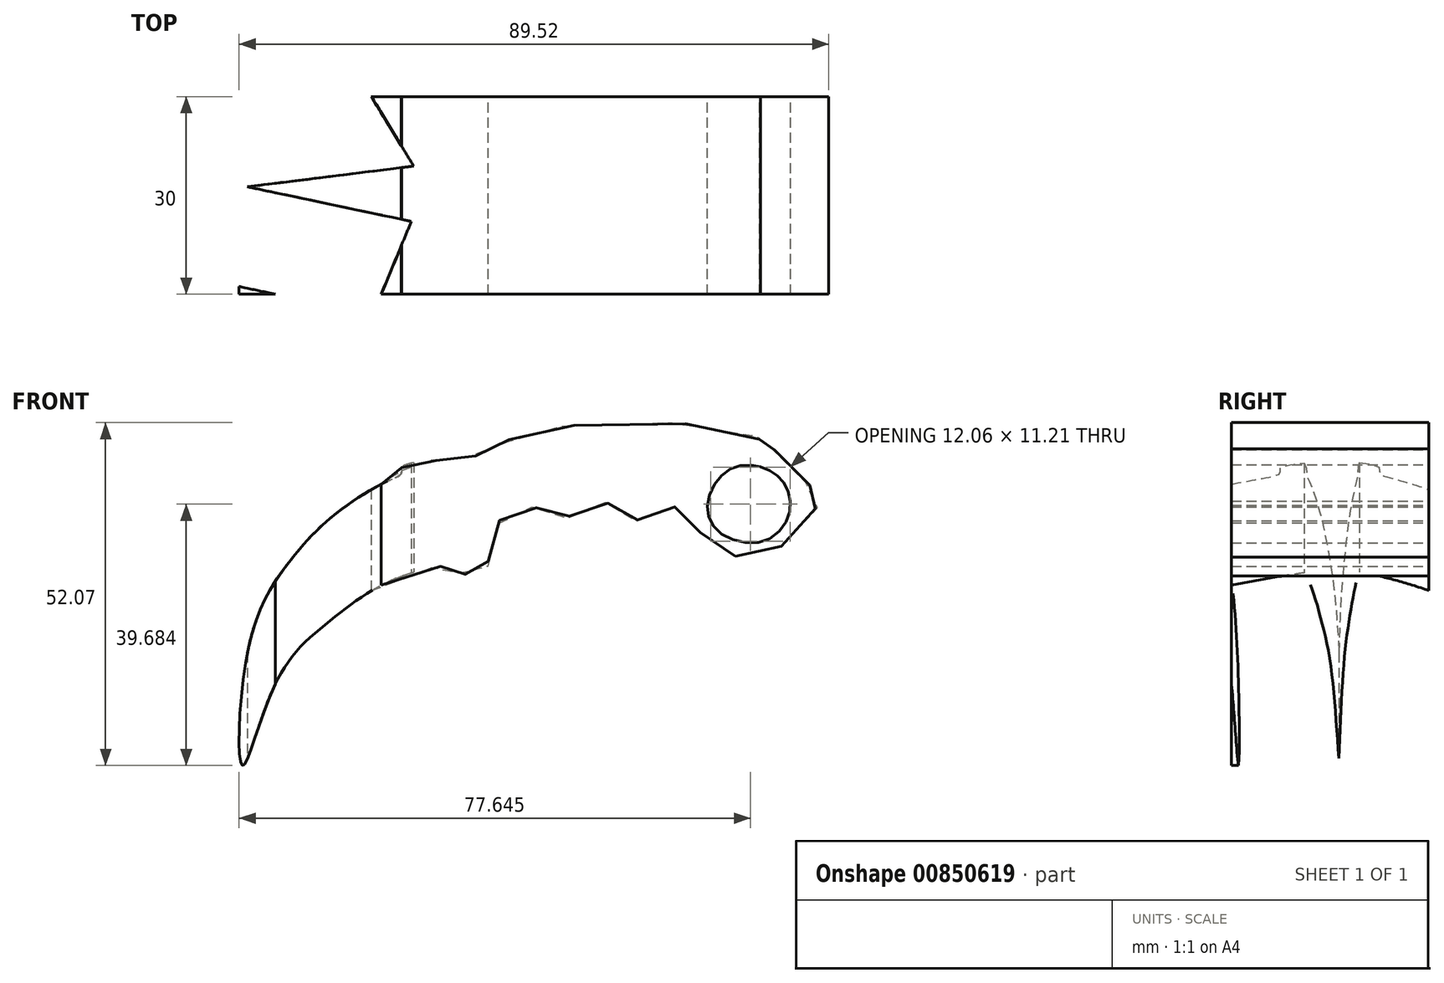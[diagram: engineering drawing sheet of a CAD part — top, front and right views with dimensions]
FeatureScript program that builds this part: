
annotation { "Feature Type Name" : "Feature", "Feature Type Description" : "" }
export const myFeature = defineFeature(function(context is Context, id is Id, definition is map)
    precondition{}
    {
        {
            var Q0;
            Q0=qCreatedBy(makeId("Front.planeOp"),FACE);
            var sketch = newSketch(context, id + "F0", { "sketchPlane" : qUnion([Q0])});
            skFitSpline(sketch, "E0", {"points": [v(33.88, 44.4) * mm, v(30.64, 46.68) * mm, v(25.88, 46.49) * mm, v(22.46, 41.73) * mm, v(23.98, 36.97) * mm, v(30.83, 35.45) * mm, v(34.83, 39.83) * mm, v(33.88, 44.4) * mm]});
            skFitSpline(sketch, "E1", {"points": [v(-48.25, 1.4) * mm, v(-43.13, 14.07) * mm, v(-34.97, 23.36) * mm, v(-27.13, 28.8) * mm, v(-17.69, 31.67) * mm, v(-15.29, 31.2) * mm, v(-15.13, 30.72) * mm, v(-11.29, 30.4) * mm, v(-10.97, 32) * mm, v(-9.7, 37.3) * mm, v(-8.41, 39.54) * mm, v(-3.45, 40.5) * mm, v(0, 38.56) * mm, v(3.27, 40.8) * mm, v(7.76, 40.96) * mm, v(10.96, 38.23) * mm, v(13.36, 40.31) * mm, v(18, 40.47) * mm, v(19.93, 38.54) * mm, v(23.61, 34.53) * mm, v(27.61, 33.08) * mm, v(33.54, 34.68) * mm, v(38.02, 39.97) * mm, v(40.74, 41.73) * mm, v(34.17, 46.7) * mm, v(32.24, 49.44) * mm, v(30.32, 49.44) * mm, v(30.32, 50.72) * mm, v(12.87, 53.47) * mm, v(-7.3, 51.24) * mm, v(-8.74, 49.96) * mm, v(-13.86, 48.2) * mm, v(-18.02, 47.73) * mm, v(-21.22, 47.57) * mm, v(-24.1, 46.61) * mm, v(-24.1, 45.8) * mm, v(-26.35, 44.53) * mm, v(-32.27, 41) * mm, v(-36.9, 37.16) * mm, v(-41.86, 31.4) * mm, v(-47.46, 18.73) * mm, v(-48.25, 1.4) * mm]});
            skSolve(sketch);
        }
        {
            var Q0;
            Q0 = qSketchRegion(id + "F0", true);
            extrude(context, id + "F1", {"entities" : qUnion([Q0]), "depth" : 30 * mm, "offsetDistance" : 25 * mm});
        }
        {
            var Q0;
            Q0=qCreatedBy(makeId("Top.planeOp"),FACE);
            var sketch = newSketch(context, id + "F2", { "sketchPlane" : qUnion([Q0])});
            skLineSegment(sketch, "E2", {"start": v(-22.61, -18.94) * mm, "end": v(-47.5, -13.69) * mm});
            skLineSegment(sketch, "E3", {"start": v(-52.35, -28.04) * mm, "end": v(-28.51, -33.2) * mm});
            skLineSegment(sketch, "E4", {"start": v(-28.51, -33.2) * mm, "end": v(-22.61, -18.94) * mm});
            skLineSegment(sketch, "E5", {"start": v(-47.5, -13.69) * mm, "end": v(-16.38, -15) * mm, "construction": true});
            skLineSegment(sketch, "E6.MirrorCS", {"start": v(-22.26, -10.54) * mm, "end": v(-47.5, -13.69) * mm});
            skLineSegment(sketch, "E7", {"start": v(-22.26, -10.54) * mm, "end": v(-40.48, 19.33) * mm});
            skLineSegment(sketch, "E8", {"start": v(-40.48, 19.33) * mm, "end": v(-68.24, 5.02) * mm});
            skLineSegment(sketch, "E9", {"start": v(-68.24, 5.02) * mm, "end": v(-52.35, -28.04) * mm});
            skLineSegment(sketch, "E10", {"start": v(-16.38, 0) * mm, "end": v(-16.38, -30) * mm, "construction": true});
            skSolve(sketch);
        }
        {
            var Q0;
            Q0 = qSketchRegion(id + "F2", true);
            extrude(context, id + "F3", {"entities" : qUnion([Q0]), "operationType" : NewBodyOperationType.REMOVE, "endBound" : BoundingType.THROUGH_ALL, "depth" : 25 * mm, "offsetDistance" : 25 * mm});
        }
        {
            var Q0;
            Q0=qCreatedBy(makeId("Top.planeOp"),FACE);
            var sketch = newSketch(context, id + "F4", { "sketchPlane" : qUnion([Q0])});
            skLineSegment(sketch, "E11", {"start": v(-40.1, -27.62) * mm, "end": v(-39.59, -31.1) * mm});
            skLineSegment(sketch, "E12", {"start": v(-43.76, -34.74) * mm, "end": v(-49.84, -33.18) * mm});
            skLineSegment(sketch, "E13", {"start": v(-49.84, -33.18) * mm, "end": v(-51.4, -30.75) * mm});
            skLineSegment(sketch, "E14", {"start": v(-51.4, -30.75) * mm, "end": v(-51.4, -27.45) * mm});
            skLineSegment(sketch, "E15", {"start": v(-51.4, -27.45) * mm, "end": v(-49.32, -27.45) * mm});
            skLineSegment(sketch, "E16", {"start": v(-49.32, -27.45) * mm, "end": v(-46.01, -25.01) * mm});
            skLineSegment(sketch, "E17", {"start": v(-46.01, -25.01) * mm, "end": v(-40.1, -27.62) * mm});
            skLineSegment(sketch, "E18", {"start": v(-39.59, -31.1) * mm, "end": v(-43.76, -35.96) * mm});
            skLineSegment(sketch, "E19", {"start": v(-43.76, -35.96) * mm, "end": v(-43.76, -34.74) * mm});
            skSolve(sketch);
        }
        {
            var Q0;
            Q0 = qSketchRegion(id + "F4", true);
            extrude(context, id + "F5", {"entities" : qUnion([Q0]), "operationType" : NewBodyOperationType.REMOVE, "oppositeDirection" : true, "depth" : 25 * mm, "offsetDistance" : 25 * mm});
        }
    });
